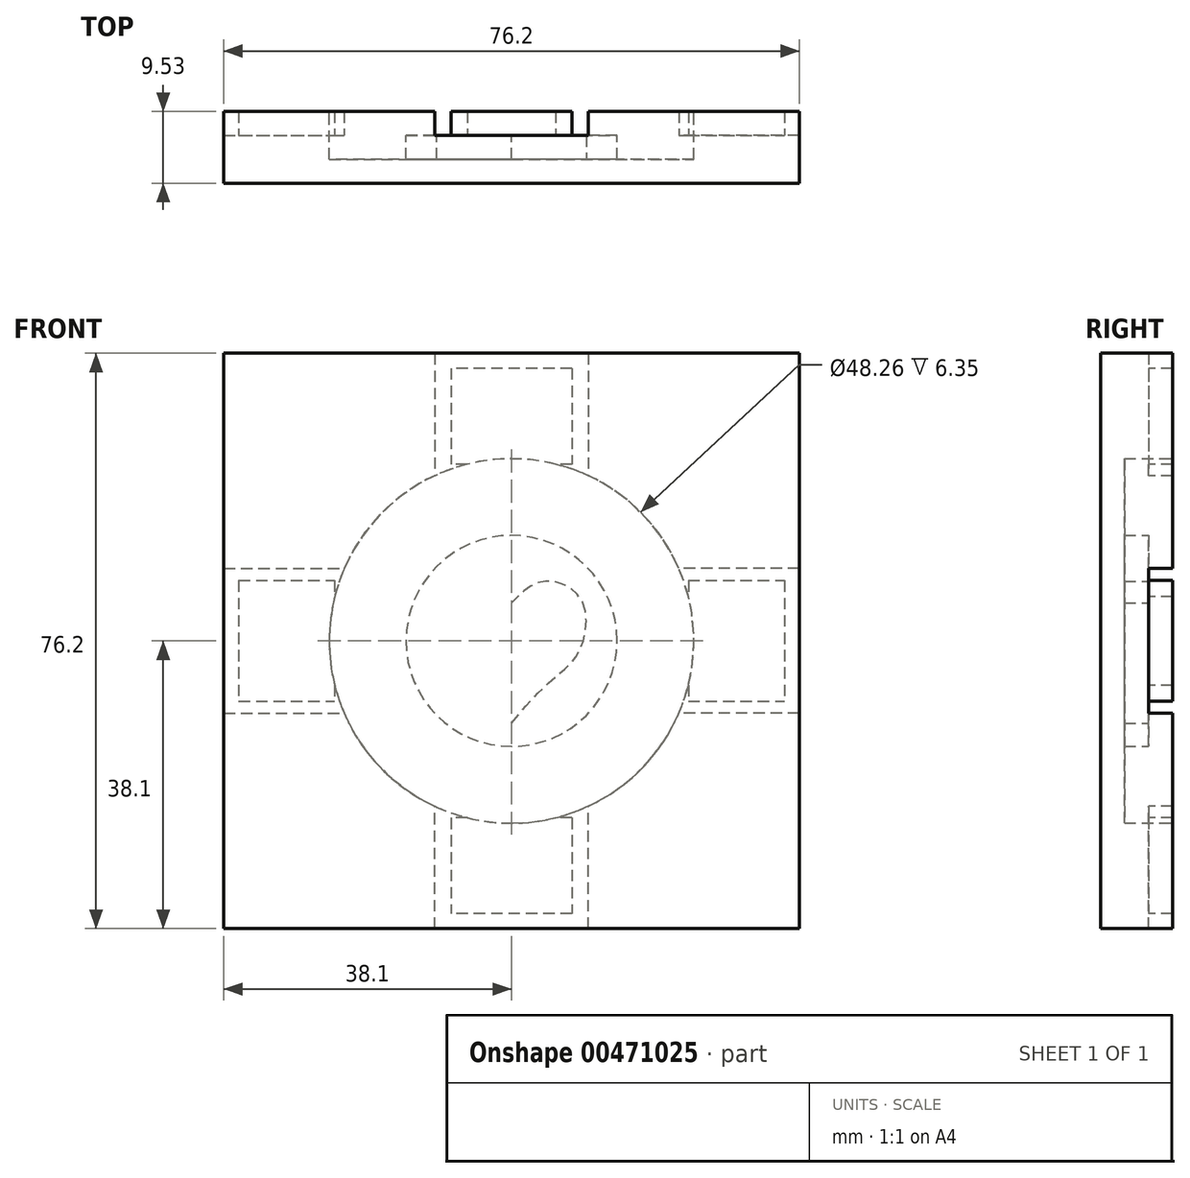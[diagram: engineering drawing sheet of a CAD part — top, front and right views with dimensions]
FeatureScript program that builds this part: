
annotation { "Feature Type Name" : "Feature", "Feature Type Description" : "" }
export const myFeature = defineFeature(function(context is Context, id is Id, definition is map)
    precondition{}
    {
        {
            var Q0;
            Q0=qCreatedBy(makeId("Front.planeOp"),FACE);
            var sketch = newSketch(context, id + "F0", { "sketchPlane" : qUnion([Q0])});
            skLineSegment(sketch, "E0.bottom", {"start": v(-38.1, 38.1) * mm, "end": v(38.1, 38.1) * mm});
            skLineSegment(sketch, "E0.top", {"start": v(-38.1, -38.1) * mm, "end": v(38.1, -38.1) * mm});
            skLineSegment(sketch, "E0.left", {"start": v(-38.1, 38.1) * mm, "end": v(-38.1, -38.1) * mm});
            skLineSegment(sketch, "E0.right", {"start": v(38.1, 38.1) * mm, "end": v(38.1, -38.1) * mm});
            skPoint(sketch, "E0.middle", {"position": v(0, 0) * mm});
            skCircle(sketch, "E1", {"center": v(0, 0) * mm, "radius": 13.97 * mm});
            skCircle(sketch, "E2.0", {"center": v(0, 0) * mm, "radius": 24.13 * mm});
            skSolve(sketch);
        }
        {
            var Q0;
            Q0 = qSketchRegion(id + "F0", true);
            var Q1;
            Q1=makeQuery(id+"F0.imprint","IMPRINT",FACE,{"disambiguationData":[TD([[makeQuery(id+"F0.imprint","IMPRINT",EDGE,{"derivedFrom":sQuery(id+"F0.wireOp",EDGE,"E1")}),-1.0]])]});
            var Q2;
            Q2=makeQuery(id+"F0.imprint","IMPRINT",FACE,{"disambiguationData":[TD([[makeQuery(id+"F0.imprint","IMPRINT",EDGE,{"derivedFrom":sQuery(id+"F0.wireOp",EDGE,"E1")}),1.0]])]});
            extrude(context, id + "F1", {"entities" : qUnion([Q0, Q1, Q2]), "depth" : 6.35 * mm});
        }
        {
            var Q0;
            Q0=makeQuery(id+"F0.imprint","IMPRINT",FACE,{"disambiguationData":[TD([[makeQuery(id+"F0.imprint","IMPRINT",EDGE,{"derivedFrom":sQuery(id+"F0.wireOp",EDGE,"E1")}),-1.0]])]});
            extrude(context, id + "F2", {"entities" : qUnion([Q0]), "operationType" : NewBodyOperationType.REMOVE, "depth" : 3.17 * mm});
        }
        {
            var Q0;
            Q0=makeQuery(id+"F0.imprint","IMPRINT",FACE,{"disambiguationData":[TD([[makeQuery(id+"F0.imprint","IMPRINT",EDGE,{"derivedFrom":sQuery(id+"F0.wireOp",EDGE,"E1")}),1.0]])]});
            var sketch = newSketch(context, id + "F3", { "sketchPlane" : qUnion([Q0])});
            skLineSegment(sketch, "E3", {"start": v(0, 15.85) * mm, "end": v(0, -16.09) * mm, "construction": true});
            skFitSpline(sketch, "E4", {"points": [v(0, -10.89) * mm, v(-8.86, -1.55) * mm, v(-9.28, 5.35) * mm, v(-4.3, 7.9) * mm, v(0, 5.03) * mm], "startDerivative": vector(-46.67, 58.76) * mm, "endDerivative": vector(18.5, -19.04) * mm});
            skFitSpline(sketch, "E5.MirrorCS", {"points": [v(0, -10.89) * mm, v(8.86, -1.55) * mm, v(9.28, 5.35) * mm, v(4.3, 7.9) * mm, v(0, 5.03) * mm], "startDerivative": vector(46.67, 58.76) * mm, "endDerivative": vector(-18.5, -19.04) * mm});
            skLineSegment(sketch, "E6.0", {"start": v(-38.1, 38.1) * mm, "end": v(-38.1, -38.1) * mm});
            skLineSegment(sketch, "E6.1", {"start": v(-38.1, 38.1) * mm, "end": v(38.1, 38.1) * mm});
            skLineSegment(sketch, "E6.2", {"start": v(38.1, 38.1) * mm, "end": v(38.1, -38.1) * mm});
            skLineSegment(sketch, "E6.3", {"start": v(-38.1, -38.1) * mm, "end": v(38.1, -38.1) * mm});
            skCircle(sketch, "E6.4", {"center": v(0, 0) * mm, "radius": 24.13 * mm});
            skCircle(sketch, "E6.5", {"center": v(0, 0) * mm, "radius": 13.97 * mm});
            skSolve(sketch);
        }
        {
            var Q0;
            Q0=makeQuery(id+"F0.imprint","IMPRINT",FACE,{"disambiguationData":[TD([[makeQuery(id+"F0.imprint","IMPRINT",EDGE,{"derivedFrom":sQuery(id+"F0.wireOp",EDGE,"E0.bottom")}),-1.0]])]});
            var sketch = newSketch(context, id + "F4", { "sketchPlane" : qUnion([Q0])});
            skLineSegment(sketch, "E7.0", {"start": v(-38.1, 38.1) * mm, "end": v(-10.16, 38.1) * mm});
            skLineSegment(sketch, "E7.1", {"start": v(-38.1, 38.1) * mm, "end": v(-38.1, 9.59) * mm});
            skArc(sketch, "E7.2", {"start": v(5.87, 23.4) * mm, "mid": v(0, 24.13) * mm, "end": v(-5.87, 23.4) * mm});
            skLineSegment(sketch, "E7.4", {"start": v(38.1, 38.1) * mm, "end": v(38.1, 9.59) * mm});
            skLineSegment(sketch, "E7.5", {"start": v(-38.1, -38.1) * mm, "end": v(-10.16, -38.1) * mm});
            skLineSegment(sketch, "E8.bottom", {"start": v(38.1, 38.1) * mm, "end": v(10.16, 38.1) * mm});
            skLineSegment(sketch, "E8.top", {"start": v(38.1, -9.59) * mm, "end": v(22.14, -9.59) * mm});
            skLineSegment(sketch, "E8.right", {"start": v(10.16, 38.1) * mm, "end": v(10.16, 21.89) * mm});
            skLineSegment(sketch, "E9.top", {"start": v(-38.1, -9.59) * mm, "end": v(-22.14, -9.59) * mm});
            skLineSegment(sketch, "E9.right", {"start": v(-10.16, 38.1) * mm, "end": v(-10.16, 21.89) * mm});
            skLineSegment(sketch, "E10.bottom", {"start": v(38.1, -38.1) * mm, "end": v(10.16, -38.1) * mm});
            skLineSegment(sketch, "E10.top", {"start": v(38.1, 9.59) * mm, "end": v(22.14, 9.59) * mm});
            skLineSegment(sketch, "E10.left", {"start": v(38.1, -38.1) * mm, "end": v(38.1, -9.59) * mm});
            skLineSegment(sketch, "E10.right", {"start": v(10.16, -38.1) * mm, "end": v(10.16, -21.89) * mm});
            skLineSegment(sketch, "E11.top", {"start": v(-38.1, 9.59) * mm, "end": v(-22.14, 9.59) * mm});
            skLineSegment(sketch, "E11.left", {"start": v(-38.1, -38.1) * mm, "end": v(-38.1, -9.59) * mm});
            skLineSegment(sketch, "E11.right", {"start": v(-10.16, -38.1) * mm, "end": v(-10.16, -21.89) * mm});
            skPoint(sketch, "E12.orphan", {"position": v(-10.16, -9.59) * mm});
            skPoint(sketch, "E13.orphan", {"position": v(10.16, -9.59) * mm});
            skPoint(sketch, "E14.orphan", {"position": v(10.16, 9.59) * mm});
            skPoint(sketch, "E15.orphan", {"position": v(-10.16, 9.59) * mm});
            skLineSegment(sketch, "E16.bottom", {"start": v(-36.1, 8) * mm, "end": v(-23.4, 8) * mm});
            skLineSegment(sketch, "E16.top", {"start": v(-36.1, -8) * mm, "end": v(-23.4, -8) * mm});
            skLineSegment(sketch, "E16.left", {"start": v(-36.1, 8) * mm, "end": v(-36.1, -8) * mm});
            skLineSegment(sketch, "E16.right", {"start": v(36.1, 8) * mm, "end": v(36.1, -8) * mm});
            skLineSegment(sketch, "E17.trimOffspring", {"start": v(23.4, 8) * mm, "end": v(36.1, 8) * mm});
            skLineSegment(sketch, "E18.trimOffspring", {"start": v(23.4, -8) * mm, "end": v(36.1, -8) * mm});
            skLineSegment(sketch, "E19.bottom", {"start": v(8, 36.1) * mm, "end": v(-8, 36.1) * mm});
            skLineSegment(sketch, "E19.top", {"start": v(8, -36.1) * mm, "end": v(-8, -36.1) * mm});
            skLineSegment(sketch, "E19.left", {"start": v(8, 36.1) * mm, "end": v(8, 23.4) * mm});
            skLineSegment(sketch, "E19.right", {"start": v(-8, 36.1) * mm, "end": v(-8, 23.4) * mm});
            skLineSegment(sketch, "E20.trimOffspring", {"start": v(-8, -23.4) * mm, "end": v(-8, -36.1) * mm});
            skLineSegment(sketch, "E21.trimOffspring", {"start": v(8, -23.4) * mm, "end": v(8, -36.1) * mm});
            skLineSegment(sketch, "E22.0", {"start": v(23.4, 8) * mm, "end": v(23.4, 5.87) * mm});
            skLineSegment(sketch, "E23.0", {"start": v(-23.4, 8) * mm, "end": v(-23.4, 5.87) * mm});
            skLineSegment(sketch, "E24.0", {"start": v(8, 23.4) * mm, "end": v(5.87, 23.4) * mm});
            skLineSegment(sketch, "E25.0", {"start": v(8, -23.4) * mm, "end": v(5.87, -23.4) * mm});
            skLineSegment(sketch, "E26.trimOffspring", {"start": v(23.4, -5.87) * mm, "end": v(23.4, -8) * mm});
            skLineSegment(sketch, "E27.trimOffspring", {"start": v(-23.4, -5.87) * mm, "end": v(-23.4, -8) * mm});
            skLineSegment(sketch, "E28.trimOffspring", {"start": v(-5.87, -23.4) * mm, "end": v(-8, -23.4) * mm});
            skLineSegment(sketch, "E29.trimOffspring", {"start": v(-5.87, 23.4) * mm, "end": v(-8, 23.4) * mm});
            skLineSegment(sketch, "E30.trimOffspring", {"start": v(10.16, 38.1) * mm, "end": v(38.1, 38.1) * mm});
            skArc(sketch, "E31.trimOffspring", {"start": v(-10.16, 21.89) * mm, "mid": v(-17.28, 16.84) * mm, "end": v(-22.14, 9.59) * mm});
            skArc(sketch, "E32.trimOffspring", {"start": v(22.14, 9.59) * mm, "mid": v(17.28, 16.84) * mm, "end": v(10.16, 21.89) * mm});
            skArc(sketch, "E33.trimOffspring", {"start": v(23.4, -5.87) * mm, "mid": v(24.13, 0) * mm, "end": v(23.4, 5.87) * mm});
            skLineSegment(sketch, "E34.trimOffspring", {"start": v(38.1, -9.59) * mm, "end": v(38.1, -38.1) * mm});
            skArc(sketch, "E35.trimOffspring", {"start": v(-5.87, -23.4) * mm, "mid": v(0, -24.13) * mm, "end": v(5.87, -23.4) * mm});
            skLineSegment(sketch, "E36.trimOffspring", {"start": v(10.16, -38.1) * mm, "end": v(38.1, -38.1) * mm});
            skArc(sketch, "E37.trimOffspring", {"start": v(10.16, -21.89) * mm, "mid": v(17.28, -16.84) * mm, "end": v(22.14, -9.59) * mm});
            skLineSegment(sketch, "E38.trimOffspring", {"start": v(-38.1, -9.59) * mm, "end": v(-38.1, -38.1) * mm});
            skArc(sketch, "E39.trimOffspring", {"start": v(-23.4, 5.87) * mm, "mid": v(-24.13, 0) * mm, "end": v(-23.4, -5.87) * mm});
            skArc(sketch, "E40.trimOffspring", {"start": v(-22.14, -9.59) * mm, "mid": v(-17.28, -16.84) * mm, "end": v(-10.16, -21.89) * mm});
            skSolve(sketch);
        }
        {
            var Q0;
            Q0 = qSketchRegion(id + "F4", true);
            extrude(context, id + "F5", {"entities" : qUnion([Q0]), "operationType" : NewBodyOperationType.ADD, "oppositeDirection" : true, "depth" : 3.17 * mm});
        }
        {
            var Q0;
            Q0=makeQuery(id+"F3.imprint","IMPRINT",FACE,{"disambiguationData":[TD([[makeQuery(id+"F3.imprint","IMPRINT",EDGE,{"derivedFrom":sQuery(id+"F3.wireOp",EDGE,"E4")}),-1.0]])]});
            extrude(context, id + "F6", {"entities" : qUnion([Q0]), "operationType" : NewBodyOperationType.REMOVE, "depth" : 3.17 * mm});
        }
    });
